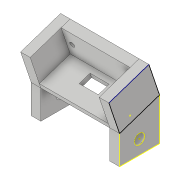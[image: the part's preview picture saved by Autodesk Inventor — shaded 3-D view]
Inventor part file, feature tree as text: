
AUTODESK INVENTOR PART (.ipt)
format: ipt  version: 2018.3 (Build 223284000, 284)  size: 236,544 bytes
history: native  units: in
note: dims shown in document units (in); Inventor stores cm internally (conversion verified against a paired STEP export)
features: extrude x13, sketch x13, plane x1
ambient origin geometry x8: Origin, YZ Plane, XZ Plane, XY Plane, X Axis, Y Axis, Z Axis, Center Point
bodies: Body1 (feature_tree)
feature tree (27):
  extrude  "Extrusion6"  Depth=0.25in TaperAngle=0.0deg
  extrude  "Extrusion8"  Depth=0.5in
  extrude  "Extrusion10"  Depth=0.65in
  extrude  "Extrusion11"  Depth=1.8in TaperAngle=0.0deg
  extrude  "Extrusion12"  TaperAngle=0.0deg  [1 undecoded]
  extrude  "Extrusion13"  Depth=1.1in
  extrude  "Extrusion14"  Depth=0.25in TaperAngle=0.0deg
  extrude  "Extrusion15"  Depth=0.125in TaperAngle=0.0deg
  extrude  "Extrusion16"  Depth=1.8in TaperAngle=0.0deg
  plane  "Work Plane1"
  extrude  "Extrusion24"  Depth=0.75in
  extrude  "Extrusion25"  Depth=0.375in
  extrude  "Extrusion26"  Depth=1.0in TaperAngle=0.0deg
  extrude  "Extrusion27"  Depth=0.75in
  sketch  "Sketch35"  dims[d137=1.0in d138=0.0in d139=0.75in d144=0.26in d145=0.3667in d146=0.5215in d147=1.0in d148=0.0in]
  sketch  "Sketch8"  dims[d40=1.8in d41=0.0in d50=0.25in d51=0.0in]
  sketch  "Sketch13"  dims[d55=0.3in d56=0.5in]
  sketch  "Sketch15"  dims[d57=0.65in d58=0.65in]
  sketch  "Sketch17"  dims[d59=1.0in d60=0.0in d62=1.8in d63=0.0in]
  sketch  "Sketch19"  dims[d67=0.25in d69=0.0in]
  sketch  "Sketch20"  dims[d70=0.0in d73=1.1in]
  sketch  "Sketch21"  dims[d76=0.0in d77=0.25in d78=0.0in]
  sketch  "Sketch22"  dims[d79=0.125in d80=0.0in d81=0.125in d82=0.0in]
  sketch  "Sketch31"  dims[d83=1.8in d84=0.0in d85=1.8in d86=0.0in]
  sketch  "Sketch32"  dims[d87=0.75in d88=0.75in]
  sketch  "Sketch33"  dims[d100=-0.1274in d132=0.375in]
  sketch  "Sketch34"  dims[d133=1.0in d134=0.0in d135=1.0in d136=0.0in]
note: 1 required parameter value undecoded (feature->parameter linkage not recoverable at this tier; creation-order binding heuristic only, values carry confidence <= 0.55)
